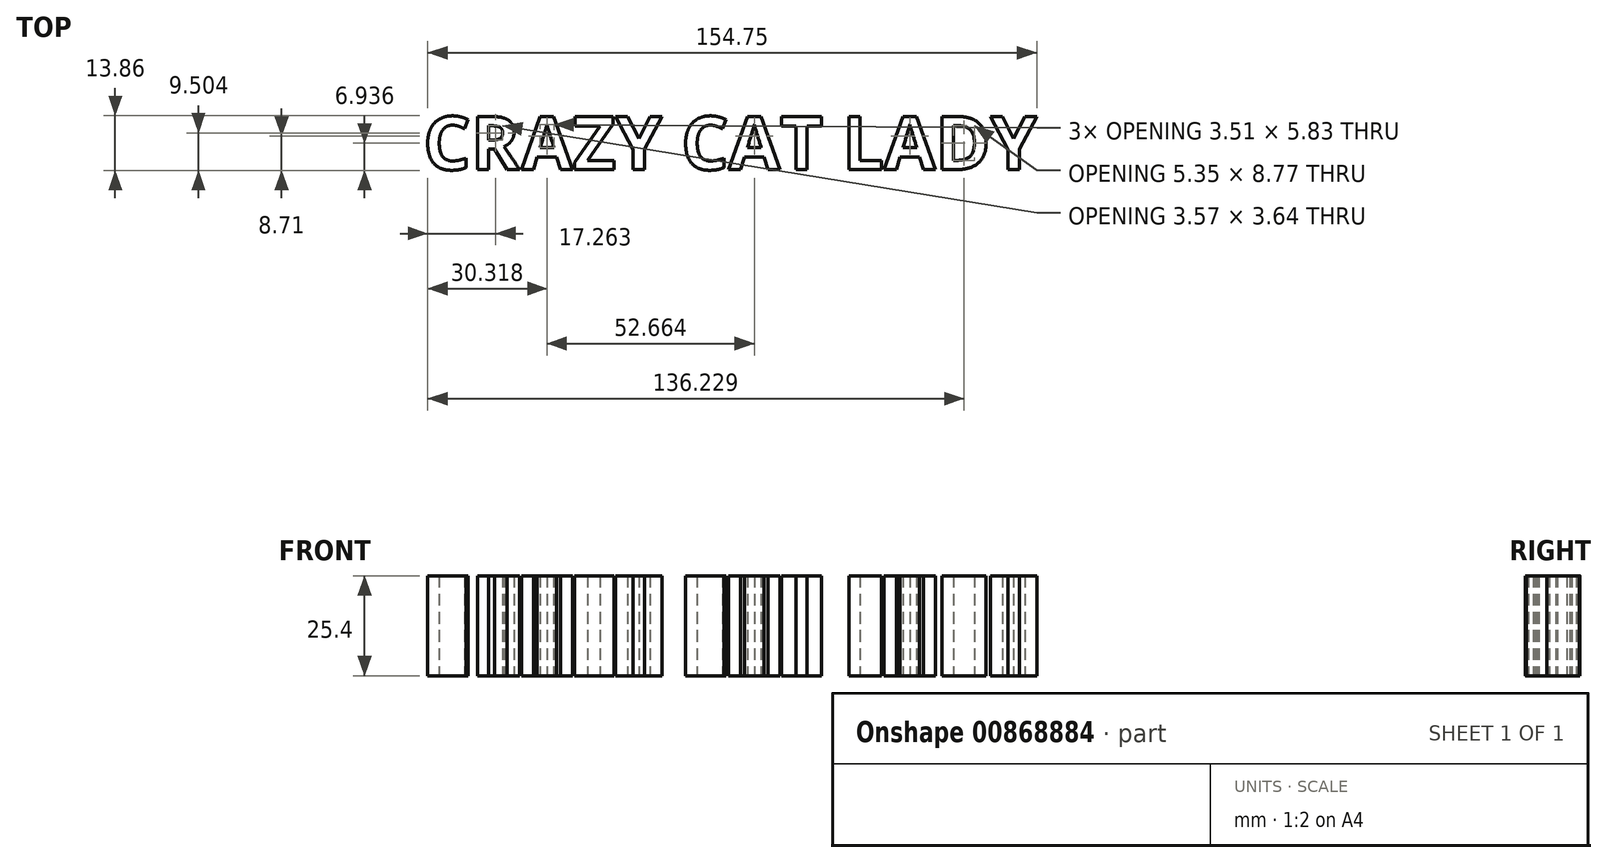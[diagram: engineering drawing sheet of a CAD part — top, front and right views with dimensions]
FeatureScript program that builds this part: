
annotation { "Feature Type Name" : "Feature", "Feature Type Description" : "" }
export const myFeature = defineFeature(function(context is Context, id is Id, definition is map)
    precondition{}
    {
        {
            var Q0;
            Q0=qCreatedBy(makeId("Top.planeOp"),FACE);
            var sketch = newSketch(context, id + "F0", { "sketchPlane" : qUnion([Q0])});
            skText(sketch, "E0", { "text": "CRAZY CAT LADY", "fontName": "OpenSans-Bold.ttf"});
            const initialGuessF0  = {"E0": [-0.0315, -0.01044, 1, 0, 0.01359]};
            skSetInitialGuess(sketch, initialGuessF0);
            skSolve(sketch);
        }
        {
            var Q0;
            Q0 = qSketchRegion(id + "F0", true);
            extrude(context, id + "F1", {"entities" : qUnion([Q0]), "depth" : 25.4 * mm, "offsetDistance" : 25.4 * mm});
        }
    });
